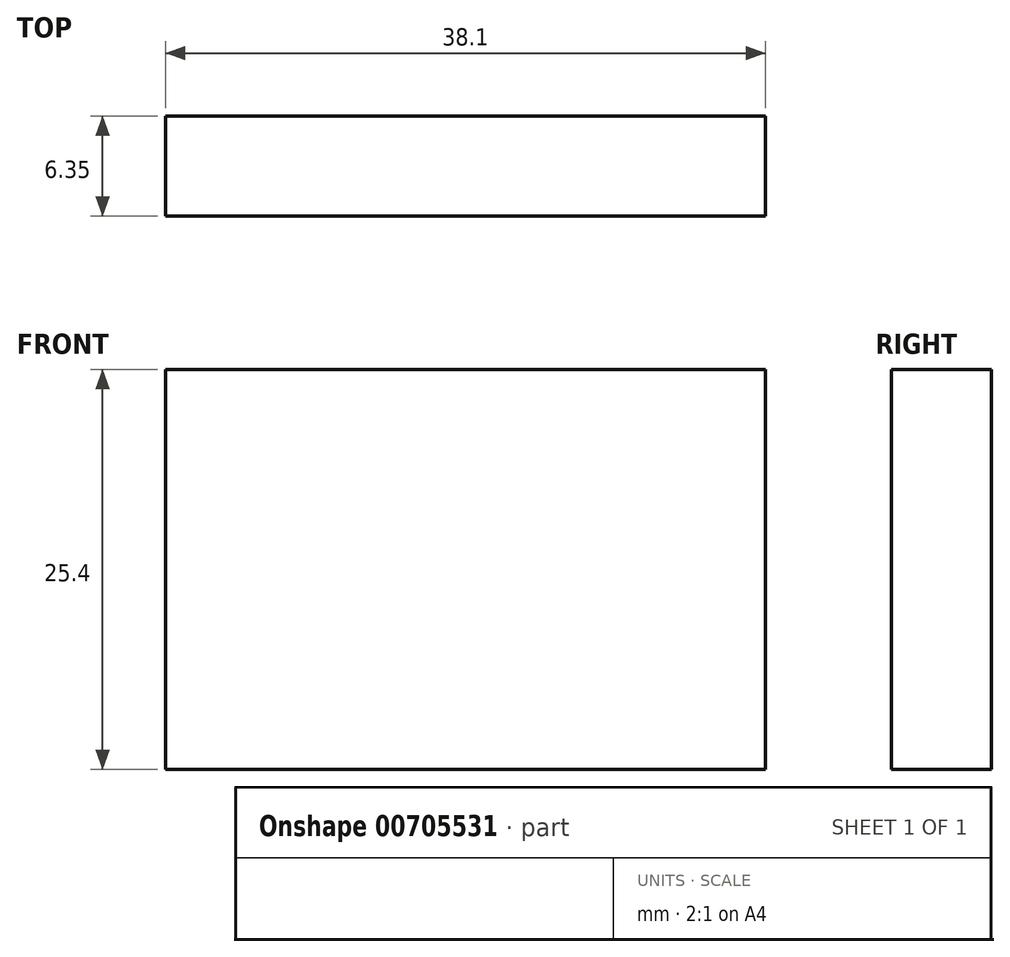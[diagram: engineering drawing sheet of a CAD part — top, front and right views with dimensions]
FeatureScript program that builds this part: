
annotation { "Feature Type Name" : "Feature", "Feature Type Description" : "" }
export const myFeature = defineFeature(function(context is Context, id is Id, definition is map)
    precondition{}
    {
        {
            var Q0;
            Q0=qCreatedBy(makeId("Front.planeOp"),FACE);
            var sketch = newSketch(context, id + "F0", { "sketchPlane" : qUnion([Q0])});
            skLineSegment(sketch, "E0.bottom", {"start": v(0, 0) * mm, "end": v(-38.1, 0) * mm});
            skLineSegment(sketch, "E0.top", {"start": v(0, 25.4) * mm, "end": v(-38.1, 25.4) * mm});
            skLineSegment(sketch, "E0.left", {"start": v(0, 0) * mm, "end": v(0, 25.4) * mm});
            skLineSegment(sketch, "E0.right", {"start": v(-38.1, 0) * mm, "end": v(-38.1, 25.4) * mm});
            skSolve(sketch);
        }
        {
            var Q0;
            Q0=makeQuery(id+"F0.imprint","IMPRINT",FACE,{"disambiguationData":[TD([[makeQuery(id+"F0.imprint","IMPRINT",EDGE,{"derivedFrom":sQuery(id+"F0.wireOp",EDGE,"E0.bottom")}),-1.0]])]});
            extrude(context, id + "F1", {"entities" : qUnion([Q0]), "depth" : 6.35 * mm, "offsetDistance" : 25.4 * mm});
        }
    });
